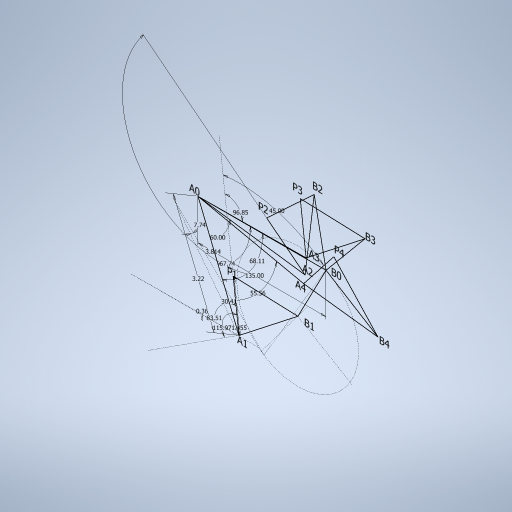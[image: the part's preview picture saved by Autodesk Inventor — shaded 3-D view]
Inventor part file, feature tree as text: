
AUTODESK INVENTOR PART (.ipt)
format: ipt  version: 2024 (Build 280153000, 153)  size: 275,968 bytes
history: native  units: in
note: dims shown in document units (in); Inventor stores cm internally (conversion verified against a paired STEP export)
features: sketch x1
ambient origin geometry x8: Origin, YZ Plane, XZ Plane, XY Plane, X Axis, Y Axis, Z Axis, Center Point
feature tree (1):
  sketch  "Sketch1"  dims[d0=0.1268in d1=0.0573in d2=0.4655in d3=0.6655in d4=45.0deg d5=60.0deg d6=0.468in d7=45.0deg d8=0.3818in d9=0.2089in d10=0.5738in d11=0.7969in d12=0.1502in d13=0.0532in d14=0.0025in]
